# Revit family: 931-20-001 DN700-750
name_source: partatom
category: Pipe Accessories
units: mm (PartAtom-declared; Revit-internal decimal feet)

## family parameters
Always vertical = Yes
Cut with Voids When Loaded = No
Part Type = Valve - Breaks Into
Round Connector Dimension = Use Diameter
Shared = No
Work Plane-Based = No

## types (4) — shared parameters
1 = 1 mm  [stored 0.00328084 ft]
2 = 3 mm  [stored 0.00984252 ft]
Actuator_FL_T = 30 mm  [stored 0.0984252 ft]
Actuator_Flange_R = 105 mm  [stored 0.344488 ft]
Body_Thickness = 2 mm  [stored 0.00656168 ft]
Body_dim = 53 mm
Body_dim1 = 116 mm
C = 165 mm  [stored 0.541339 ft]
DN700_PN10 = 931-700-20-010020200000
DN700_PN16 = 931-700-20-020020200000
DN750_PN10 = 931-750-20-010020200000
DN750_PN16 = 931-750-20-020020200000
Description_ = AVK BUTTERFLY VALVE, LUG, PN10/16
F = 68 mm  [stored 0.223097 ft]
G = 46 mm  [stored 0.150919 ft]
H = 105 mm  [stored 0.344488 ft]
Hole = 51 mm
Search_table = 931-20-001 DN700-750
URL_product_pages = https://www.avkvalves.com
base = 58 mm
base1 = 33 mm  [stored 0.108268 ft]
disk1 = 44 mm  [stored 0.144357 ft]
disk11 = 57 mm  [stored 0.187008 ft]
hole1 = 23 mm  [stored 0.0754593 ft]
wafer = 158 mm
wafer_dim2 = 158 mm
wafer_fillet = 79 mm
zero-valued in all types: DISK, Default Elevation

## per-type parameters (varying)
| type | B | B1 | Body_thickness | Bore_R | D | DN | E | Flange_R | Flange_T | Hole1 | PCD_R | Slot_dim | base_dis | disk | disk2 | disk22 | rubber | support | wafer_F | wafer_dim1 |
| DN700_PN10 | 341 mm | 342 mm | 359 mm | 350 mm  [stored 1.14829 ft] | 397 mm | 700 mm | 565 mm | 410 mm  [stored 1.34514 ft] | 33 mm  [stored 0.108268 ft] | 23 mm  [stored 0.0754593 ft] | 420 mm  [stored 1.37795 ft] | 43 mm  [stored 0.141076 ft] | 468 mm | 25 mm  [stored 0.082021 ft] | 681 mm | 33 mm  [stored 0.108268 ft] | 23 mm  [stored 0.0754593 ft] | 500 mm | 45 mm  [stored 0.147638 ft] | 33 mm  [stored 0.108268 ft] |
| DN700_PN16 | 341 mm | 342 mm | 359 mm | 350 mm  [stored 1.14829 ft] | 397 mm | 700 mm | 565 mm | 410 mm  [stored 1.34514 ft] | 40 mm  [stored 0.131234 ft] | 23 mm  [stored 0.0754593 ft] | 420 mm  [stored 1.37795 ft] | 43 mm  [stored 0.141076 ft] | 468 mm | 26 mm | 681 mm | 34 mm  [stored 0.111549 ft] | 23 mm  [stored 0.0754593 ft] | 500 mm | 45 mm  [stored 0.147638 ft] | 40 mm  [stored 0.131234 ft] |
| DN750_PN10 | 372 mm | 373 mm | 391 mm | 375 mm  [stored 1.23031 ft] | 438 mm | 750 mm | 584 mm | 430 mm | 40 mm  [stored 0.131234 ft] | 24 mm  [stored 0.0787402 ft] | 470 mm | 45 mm  [stored 0.147638 ft] | 516 mm | 26 mm | 743 mm | 34 mm  [stored 0.111549 ft] | 31 mm  [stored 0.101706 ft] | 510 mm | 46 mm  [stored 0.150919 ft] | 40 mm  [stored 0.131234 ft] |
| DN750_PN16 | 372 mm | 373 mm | 391 mm | 375 mm  [stored 1.23031 ft] | 438 mm | 750 mm | 584 mm | 425 mm  [stored 1.39436 ft] | 40 mm  [stored 0.131234 ft] | 24 mm  [stored 0.0787402 ft] | 470 mm | 45 mm  [stored 0.147638 ft] | 516 mm | 26 mm | 743 mm | 34 mm  [stored 0.111549 ft] | 31 mm  [stored 0.101706 ft] | 510 mm | 46 mm  [stored 0.150919 ft] | 40 mm  [stored 0.131234 ft] |

note: [stored X ft] marks values corroborated as IEEE doubles in the binary element streams (Revit-internal decimal feet)

## geometry (parser evidence)
native form markers: Sweep x5
no freeform markers — native parametric forms only
